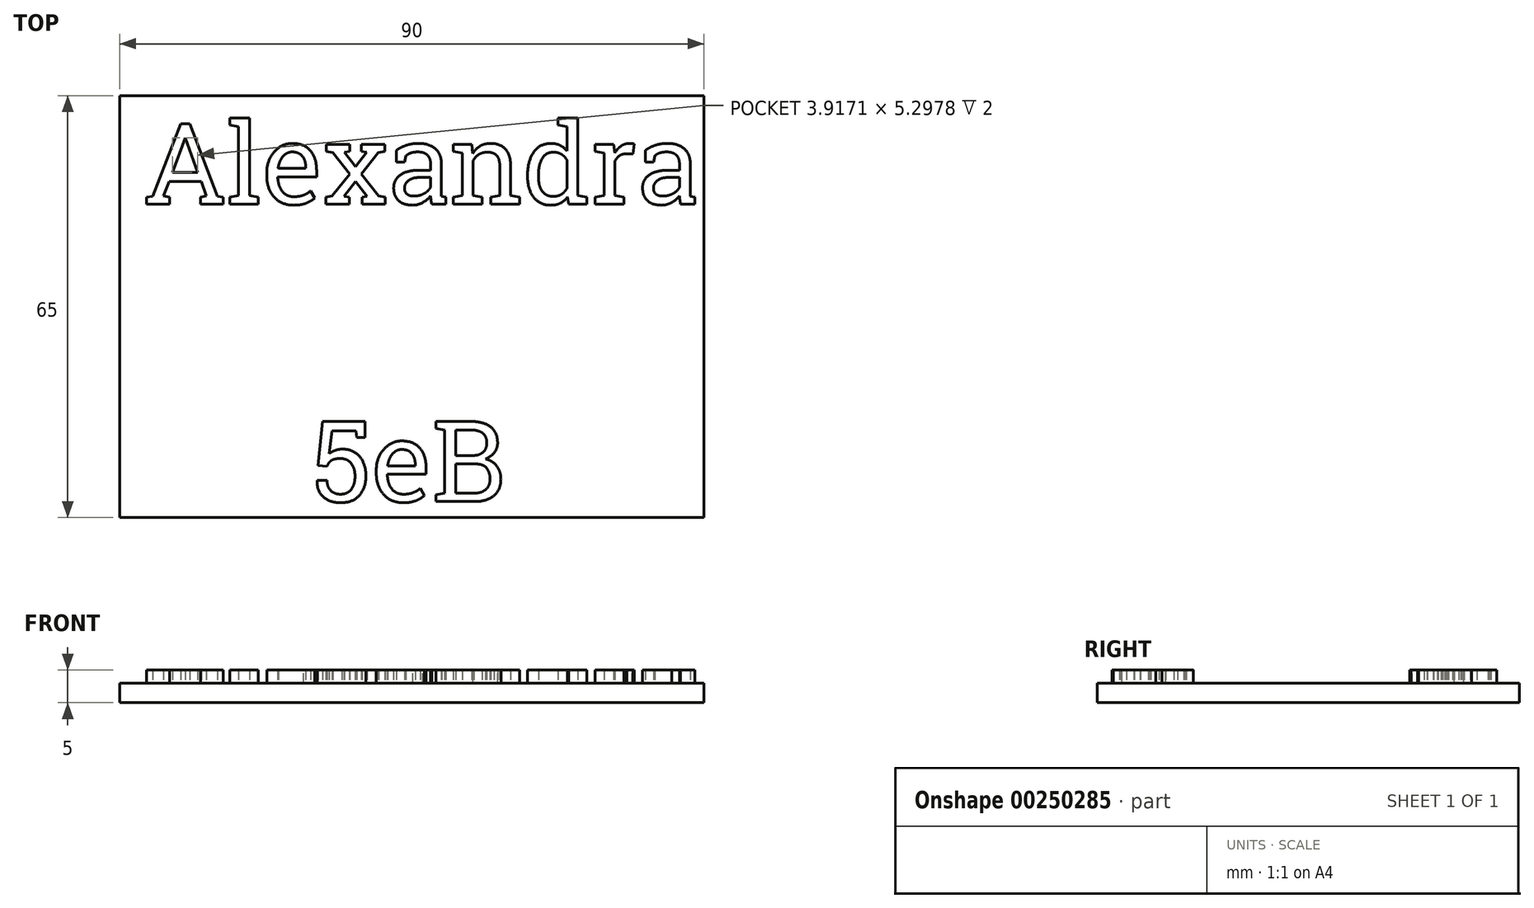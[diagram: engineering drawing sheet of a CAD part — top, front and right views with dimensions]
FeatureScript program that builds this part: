
annotation { "Feature Type Name" : "Feature", "Feature Type Description" : "" }
export const myFeature = defineFeature(function(context is Context, id is Id, definition is map)
    precondition{}
    {
        {
            var Q0;
            Q0=qCreatedBy(makeId("Top.planeOp"),FACE);
            var sketch = newSketch(context, id + "F0", { "sketchPlane" : qUnion([Q0])});
            skLineSegment(sketch, "E0.bottom", {"start": v(0, 0) * mm, "end": v(90, 0) * mm});
            skLineSegment(sketch, "E0.top", {"start": v(0, -65) * mm, "end": v(90, -65) * mm});
            skLineSegment(sketch, "E0.left", {"start": v(0, 0) * mm, "end": v(0, -65) * mm});
            skLineSegment(sketch, "E0.right", {"start": v(90, 0) * mm, "end": v(90, -65) * mm});
            skSolve(sketch);
        }
        {
            var Q0;
            Q0=makeQuery(id+"F0.imprint","IMPRINT",FACE,{"disambiguationData":[TD([[makeQuery(id+"F0.imprint","IMPRINT",EDGE,{"derivedFrom":sQuery(id+"F0.wireOp",EDGE,"E0.bottom")}),-1.0]])]});
            extrude(context, id + "F1", {"entities" : qUnion([Q0]), "depth" : 3 * mm});
        }
        {
            var Q0;
            Q0=makeQuery(id+"F1.opExtrude","CAP_FACE",FACE,{"disambiguationData":[OSD([sQuery(id+"F0.wireOp",EDGE,"E0.bottom"),sQuery(id+"F0.wireOp",EDGE,"E0.top"),sQuery(id+"F0.wireOp",EDGE,"E0.left"),sQuery(id+"F0.wireOp",EDGE,"E0.right")])],"isStart":false});
            var sketch = newSketch(context, id + "F2", { "sketchPlane" : qUnion([Q0])});
            skText(sketch, "E1", { "text": "Alexandra\n     \n      5eB", "fontName": "RobotoSlab-Regular.ttf"});
            const initialGuessF2  = {"E1": [0.0037, -0.0167, 1, 0, 0.0125]};
            skSetInitialGuess(sketch, initialGuessF2);
            skSolve(sketch);
        }
        {
            var Q0;
            Q0 = qSketchRegion(id + "F2", true);
            extrude(context, id + "F3", {"entities" : qUnion([Q0]), "operationType" : NewBodyOperationType.ADD, "depth" : 2 * mm});
        }
    });
